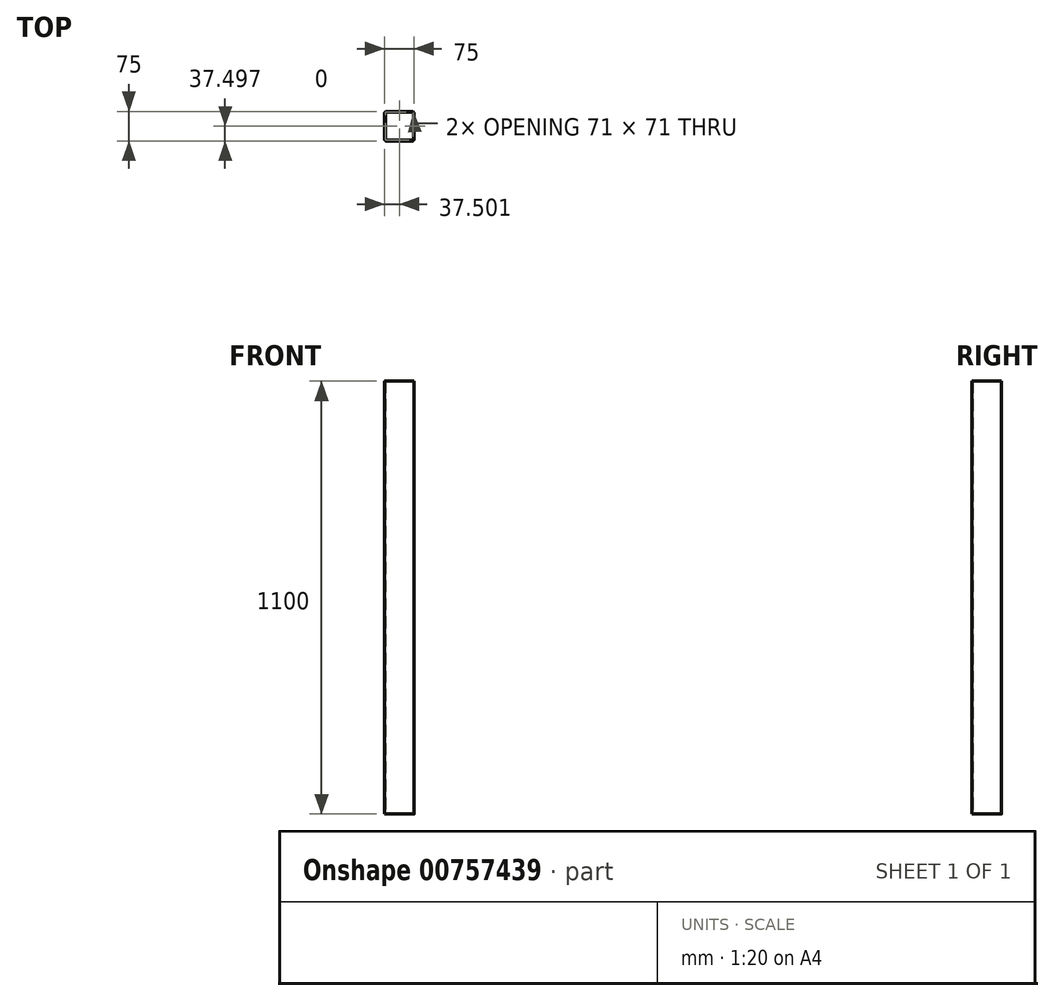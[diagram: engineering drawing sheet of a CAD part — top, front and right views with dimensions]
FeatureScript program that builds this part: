
annotation { "Feature Type Name" : "Feature", "Feature Type Description" : "" }
export const myFeature = defineFeature(function(context is Context, id is Id, definition is map)
    precondition{}
    {
        {
            var Q0;
            Q0=qCreatedBy(makeId("Top.planeOp"),FACE);
            var sketch = newSketch(context, id + "F0", { "sketchPlane" : qUnion([Q0])});
            skLineSegment(sketch, "E0.bottom", {"start": v(-33.59, 33.8) * mm, "end": v(31.41, 33.8) * mm});
            skLineSegment(sketch, "E0.top", {"start": v(-33.59, -41.2) * mm, "end": v(31.41, -41.2) * mm});
            skLineSegment(sketch, "E0.left", {"start": v(-38.59, 28.8) * mm, "end": v(-38.59, -36.2) * mm});
            skLineSegment(sketch, "E0.right", {"start": v(36.41, 28.8) * mm, "end": v(36.41, -36.2) * mm});
            skPoint(sketch, "E1.visualSharp", {"position": v(-38.59, 33.8) * mm});
            skArc(sketch, "E1.filletArc", {"start": v(-33.59, 33.8) * mm, "mid": v(-37.12, 32.33) * mm, "end": v(-38.59, 28.8) * mm});
            skPoint(sketch, "E2.visualSharp", {"position": v(36.41, 33.8) * mm});
            skArc(sketch, "E2.filletArc", {"start": v(36.41, 28.8) * mm, "mid": v(34.95, 32.33) * mm, "end": v(31.41, 33.8) * mm});
            skPoint(sketch, "E3.visualSharp", {"position": v(36.41, -41.2) * mm});
            skArc(sketch, "E3.filletArc", {"start": v(31.41, -41.2) * mm, "mid": v(34.95, -39.74) * mm, "end": v(36.41, -36.2) * mm});
            skPoint(sketch, "E4.visualSharp", {"position": v(-38.59, -41.2) * mm});
            skArc(sketch, "E4.filletArc", {"start": v(-38.59, -36.2) * mm, "mid": v(-37.12, -39.74) * mm, "end": v(-33.59, -41.2) * mm});
            skLineSegment(sketch, "E5.0", {"start": v(-33.59, -39.2) * mm, "end": v(31.41, -39.2) * mm});
            skLineSegment(sketch, "E5.1", {"start": v(-36.59, 28.8) * mm, "end": v(-36.59, -36.2) * mm});
            skLineSegment(sketch, "E5.2", {"start": v(-33.59, 31.8) * mm, "end": v(31.41, 31.8) * mm});
            skLineSegment(sketch, "E5.3", {"start": v(34.41, 28.8) * mm, "end": v(34.41, -36.2) * mm});
            skPoint(sketch, "E6.visualSharp", {"position": v(-36.59, -39.2) * mm});
            skArc(sketch, "E6.filletArc", {"start": v(-36.59, -36.2) * mm, "mid": v(-35.71, -38.32) * mm, "end": v(-33.59, -39.2) * mm});
            skPoint(sketch, "E7.visualSharp", {"position": v(34.41, 31.8) * mm});
            skArc(sketch, "E7.filletArc", {"start": v(34.41, 28.8) * mm, "mid": v(33.53, 30.92) * mm, "end": v(31.41, 31.8) * mm});
            skPoint(sketch, "E8.visualSharp", {"position": v(-36.59, 31.8) * mm});
            skArc(sketch, "E8.filletArc", {"start": v(-33.59, 31.8) * mm, "mid": v(-35.71, 30.92) * mm, "end": v(-36.59, 28.8) * mm});
            skPoint(sketch, "E9.visualSharp", {"position": v(34.41, -39.2) * mm});
            skArc(sketch, "E9.filletArc", {"start": v(31.41, -39.2) * mm, "mid": v(33.53, -38.32) * mm, "end": v(34.41, -36.2) * mm});
            skSolve(sketch);
        }
        {
            var Q0;
            Q0 = qSketchRegion(id + "F0", true);
            extrude(context, id + "F1", {"entities" : qUnion([Q0]), "depth" : 1100 * mm, "offsetDistance" : 25 * mm});
        }
    });
